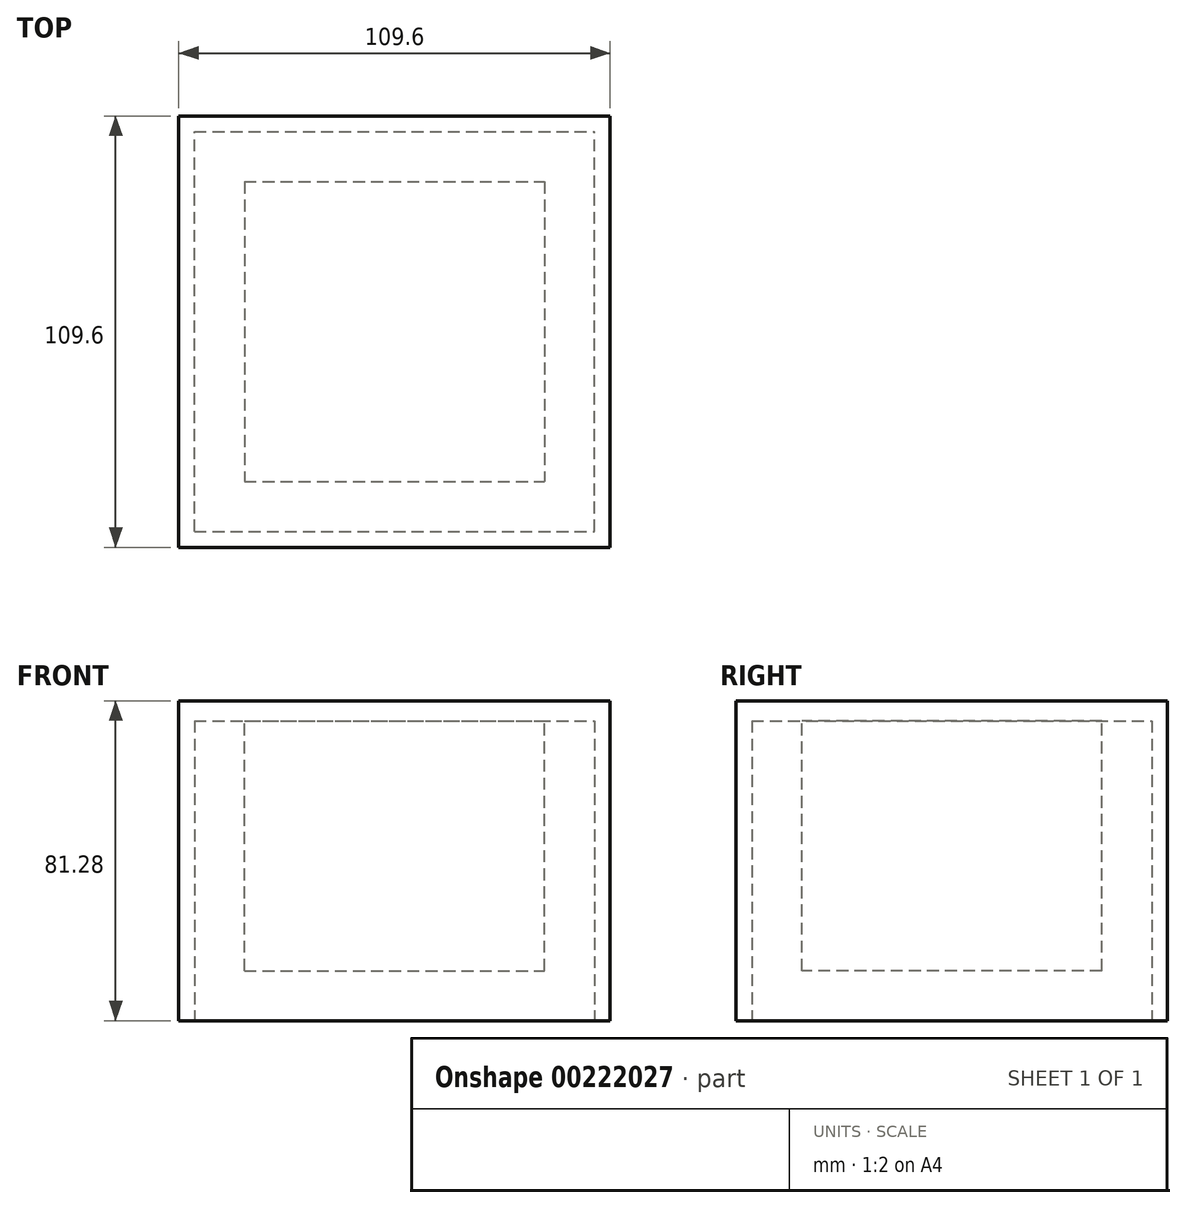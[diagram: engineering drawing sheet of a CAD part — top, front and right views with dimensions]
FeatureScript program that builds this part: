
annotation { "Feature Type Name" : "Feature", "Feature Type Description" : "" }
export const myFeature = defineFeature(function(context is Context, id is Id, definition is map)
    precondition{}
    {
        {
            var Q0;
            Q0=qCreatedBy(makeId("Top.planeOp"),FACE);
            var sketch = newSketch(context, id + "F0", { "sketchPlane" : qUnion([Q0])});
            skLineSegment(sketch, "E0.bottom", {"start": v(0, 0) * mm, "end": v(101.6, 0) * mm});
            skLineSegment(sketch, "E0.top", {"start": v(0, 101.6) * mm, "end": v(101.6, 101.6) * mm});
            skLineSegment(sketch, "E0.left", {"start": v(0, 0) * mm, "end": v(0, 101.6) * mm});
            skLineSegment(sketch, "E0.right", {"start": v(101.6, 0) * mm, "end": v(101.6, 101.6) * mm});
            skSolve(sketch);
        }
        {
            var Q0;
            Q0 = qSketchRegion(id + "F0", true);
            extrude(context, id + "F1", {"entities" : qUnion([Q0]), "depth" : 76.2 * mm});
        }
        {
            var Q0;
            Q0=makeQuery(id+"F1.opExtrude","CAP_FACE",FACE,{"disambiguationData":[OSD([sQuery(id+"F0.wireOp",EDGE,"E0.bottom"),sQuery(id+"F0.wireOp",EDGE,"E0.top"),sQuery(id+"F0.wireOp",EDGE,"E0.left"),sQuery(id+"F0.wireOp",EDGE,"E0.right")])],"isStart":false});
            var sketch = newSketch(context, id + "F2", { "sketchPlane" : qUnion([Q0])});
            skLineSegment(sketch, "E1.bottom", {"start": v(12.7, 88.9) * mm, "end": v(88.9, 88.9) * mm});
            skLineSegment(sketch, "E1.top", {"start": v(12.7, 12.7) * mm, "end": v(88.9, 12.7) * mm});
            skLineSegment(sketch, "E1.left", {"start": v(12.7, 88.9) * mm, "end": v(12.7, 12.7) * mm});
            skLineSegment(sketch, "E1.right", {"start": v(88.9, 88.9) * mm, "end": v(88.9, 12.7) * mm});
            skSolve(sketch);
        }
        {
            var Q0;
            Q0 = qSketchRegion(id + "F2", true);
            extrude(context, id + "F3", {"entities" : qUnion([Q0]), "operationType" : NewBodyOperationType.REMOVE, "oppositeDirection" : true, "depth" : 63.5 * mm});
        }
        {
            var Q0;
            Q0=qCreatedBy(makeId("Top.planeOp"),FACE);
            var sketch = newSketch(context, id + "F4", { "sketchPlane" : qUnion([Q0])});
            skLineSegment(sketch, "E2.bottom", {"start": v(-4, 105.6) * mm, "end": v(105.6, 105.6) * mm});
            skLineSegment(sketch, "E2.top", {"start": v(-4, -4) * mm, "end": v(105.6, -4) * mm});
            skLineSegment(sketch, "E2.left", {"start": v(-4, 105.6) * mm, "end": v(-4, -4) * mm});
            skLineSegment(sketch, "E2.right", {"start": v(105.6, 105.6) * mm, "end": v(105.6, -4) * mm});
            skSolve(sketch);
        }
        {
            var Q0;
            Q0 = qSketchRegion(id + "F4", true);
            extrude(context, id + "F5", {"entities" : qUnion([Q0]), "depth" : 81.28 * mm});
        }
        {
            var Q0;
            Q0=makeQuery(id+"F1.opExtrude","SWEPT_BODY",BODY,{"disambiguationData":[OSD([sQuery(id+"F0.wireOp",EDGE,"E0.bottom"),sQuery(id+"F0.wireOp",EDGE,"E0.top"),sQuery(id+"F0.wireOp",EDGE,"E0.left"),sQuery(id+"F0.wireOp",EDGE,"E0.right")])]});
            var Q1;
            Q1=makeQuery(id+"F5.opExtrude","SWEPT_BODY",BODY,{"disambiguationData":[OSD([sQuery(id+"F4.wireOp",EDGE,"E2.bottom"),sQuery(id+"F4.wireOp",EDGE,"E2.top"),sQuery(id+"F4.wireOp",EDGE,"E2.left"),sQuery(id+"F4.wireOp",EDGE,"E2.right")])]});
            booleanBodies(context, id + "F6", {"operationType" : BooleanOperationType.SUBTRACTION, "tools" : qUnion([Q0]), "targets" : qUnion([Q1])});
        }
    });
